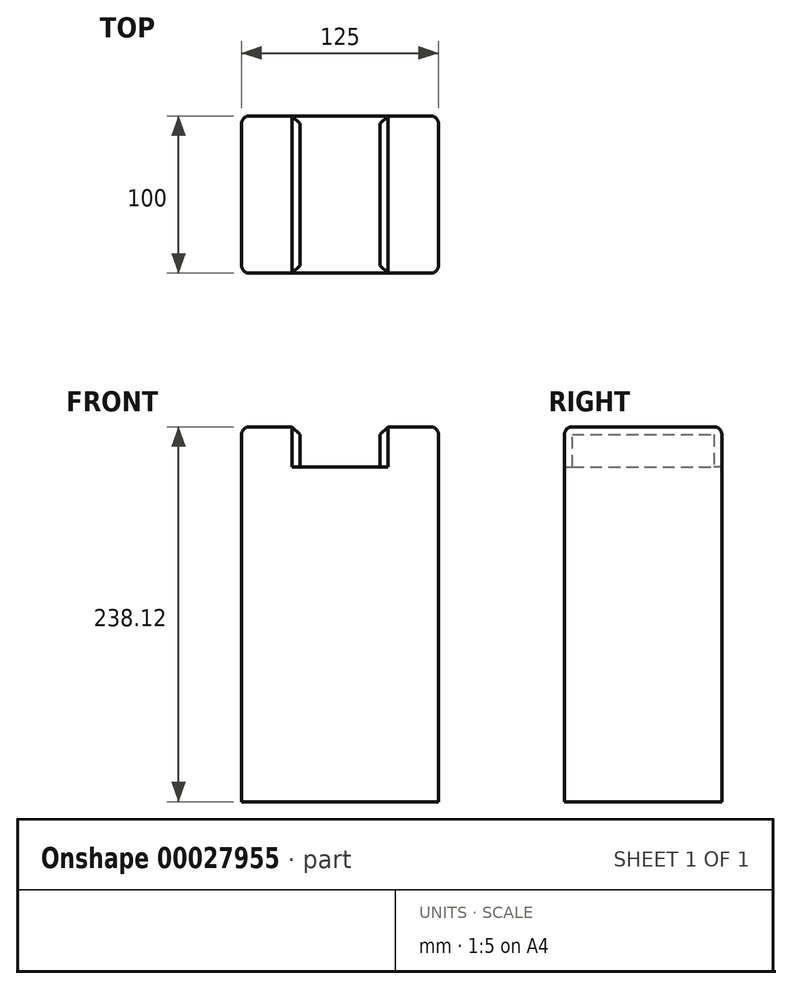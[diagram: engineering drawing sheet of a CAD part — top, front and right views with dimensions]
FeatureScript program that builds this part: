
annotation { "Feature Type Name" : "Feature", "Feature Type Description" : "" }
export const myFeature = defineFeature(function(context is Context, id is Id, definition is map)
    precondition{}
    {
        {
            var Q0;
            Q0=qCreatedBy(makeId("Front.planeOp"),FACE);
            var sketch = newSketch(context, id + "F0", { "sketchPlane" : qUnion([Q0])});
            skLineSegment(sketch, "E0.bottom", {"start": v(-62.5, 119.06) * mm, "end": v(62.5, 119.06) * mm, "construction": true});
            skLineSegment(sketch, "E0.top", {"start": v(-62.5, -119.06) * mm, "end": v(62.5, -119.06) * mm});
            skLineSegment(sketch, "E0.left", {"start": v(-62.5, 119.06) * mm, "end": v(-62.5, -119.06) * mm});
            skLineSegment(sketch, "E0.right", {"start": v(62.5, 119.06) * mm, "end": v(62.5, -119.06) * mm});
            skPoint(sketch, "E0.middle", {"position": v(0, 0) * mm});
            skLineSegment(sketch, "E1.bottom", {"start": v(-25.4, 119.06) * mm, "end": v(25.4, 119.06) * mm, "construction": true});
            skLineSegment(sketch, "E1.top", {"start": v(-25.4, 93.66) * mm, "end": v(25.4, 93.66) * mm});
            skLineSegment(sketch, "E1.left", {"start": v(-25.4, 119.06) * mm, "end": v(-25.4, 93.66) * mm});
            skLineSegment(sketch, "E1.right", {"start": v(25.4, 119.06) * mm, "end": v(25.4, 93.66) * mm});
            skPoint(sketch, "E1.middle", {"position": v(0, 106.36) * mm});
            skLineSegment(sketch, "E2", {"start": v(-62.5, 119.06) * mm, "end": v(-25.4, 119.06) * mm});
            skLineSegment(sketch, "E3", {"start": v(25.4, 119.06) * mm, "end": v(62.5, 119.06) * mm});
            skSolve(sketch);
        }
        {
            var Q0;
            Q0=makeQuery(id+"F0.imprint","IMPRINT",FACE,{"disambiguationData":[TD([[makeQuery(id+"F0.imprint","IMPRINT",EDGE,{"derivedFrom":sQuery(id+"F0.wireOp",EDGE,"E0.top")}),1.0]])]});
            extrude(context, id + "F1", {"entities" : qUnion([Q0]), "depth" : 100 * mm});
        }
        {
            var Q0;
            Q0=makeQuery(id+"F1.opExtrude","CAP_EDGE",EDGE,{"disambiguationData":[OSD([sQuery(id+"F0.wireOp",EDGE,"E2")])],"isStart":true});
            var Q1;
            Q1=makeQuery(id+"F1.opExtrude","SWEPT_EDGE",EDGE,{"disambiguationData":[OSD([sQuery(id+"F0.wireOp",EDGE,"E0.left"),sQuery(id+"F0.wireOp",EDGE,"E2")])]});
            var Q2;
            Q2=makeQuery(id+"F1.opExtrude","CAP_EDGE",EDGE,{"disambiguationData":[OSD([sQuery(id+"F0.wireOp",EDGE,"E2")])],"isStart":false});
            var Q3;
            Q3=makeQuery(id+"F1.opExtrude","CAP_EDGE",EDGE,{"disambiguationData":[OSD([sQuery(id+"F0.wireOp",EDGE,"E3")])],"isStart":false});
            var Q4;
            Q4=makeQuery(id+"F1.opExtrude","SWEPT_EDGE",EDGE,{"disambiguationData":[OSD([sQuery(id+"F0.wireOp",EDGE,"E0.right"),sQuery(id+"F0.wireOp",EDGE,"E3")])]});
            var Q5;
            Q5=makeQuery(id+"F1.opExtrude","CAP_EDGE",EDGE,{"disambiguationData":[OSD([sQuery(id+"F0.wireOp",EDGE,"E3")])],"isStart":true});
            var Q6;
            Q6=makeQuery(id+"F1.opExtrude","CAP_EDGE",EDGE,{"disambiguationData":[OSD([sQuery(id+"F0.wireOp",EDGE,"E0.right")])],"isStart":false});
            var Q7;
            Q7=makeQuery(id+"F1.opExtrude","CAP_EDGE",EDGE,{"disambiguationData":[OSD([sQuery(id+"F0.wireOp",EDGE,"E0.right")])],"isStart":true});
            var Q8;
            Q8=makeQuery(id+"F1.opExtrude","CAP_EDGE",EDGE,{"disambiguationData":[OSD([sQuery(id+"F0.wireOp",EDGE,"E0.left")])],"isStart":false});
            var Q9;
            Q9=makeQuery(id+"F1.opExtrude","CAP_EDGE",EDGE,{"disambiguationData":[OSD([sQuery(id+"F0.wireOp",EDGE,"E0.left")])],"isStart":true});
            fillet(context, id + "F2", {"entities" : qUnion([Q0, Q1, Q2, Q3, Q4, Q5, Q6, Q7, Q8, Q9]), "radius" : 5 * mm, "tangentPropagation" : true, "allowEdgeOverflow" : false});
        }
        {
            var Q0;
            Q0=makeQuery(id+"F1.opExtrude","CAP_EDGE",EDGE,{"disambiguationData":[OSD([sQuery(id+"F0.wireOp",EDGE,"E1.right")])],"isStart":false});
            var Q1;
            Q1=makeQuery(id+"F1.opExtrude","CAP_EDGE",EDGE,{"disambiguationData":[OSD([sQuery(id+"F0.wireOp",EDGE,"E1.left")])],"isStart":true});
            chamfer(context, id + "F3", {"entities" : qUnion([Q0, Q1]), "width" : 5 * mm, "tangentPropagation" : true});
        }
    });
